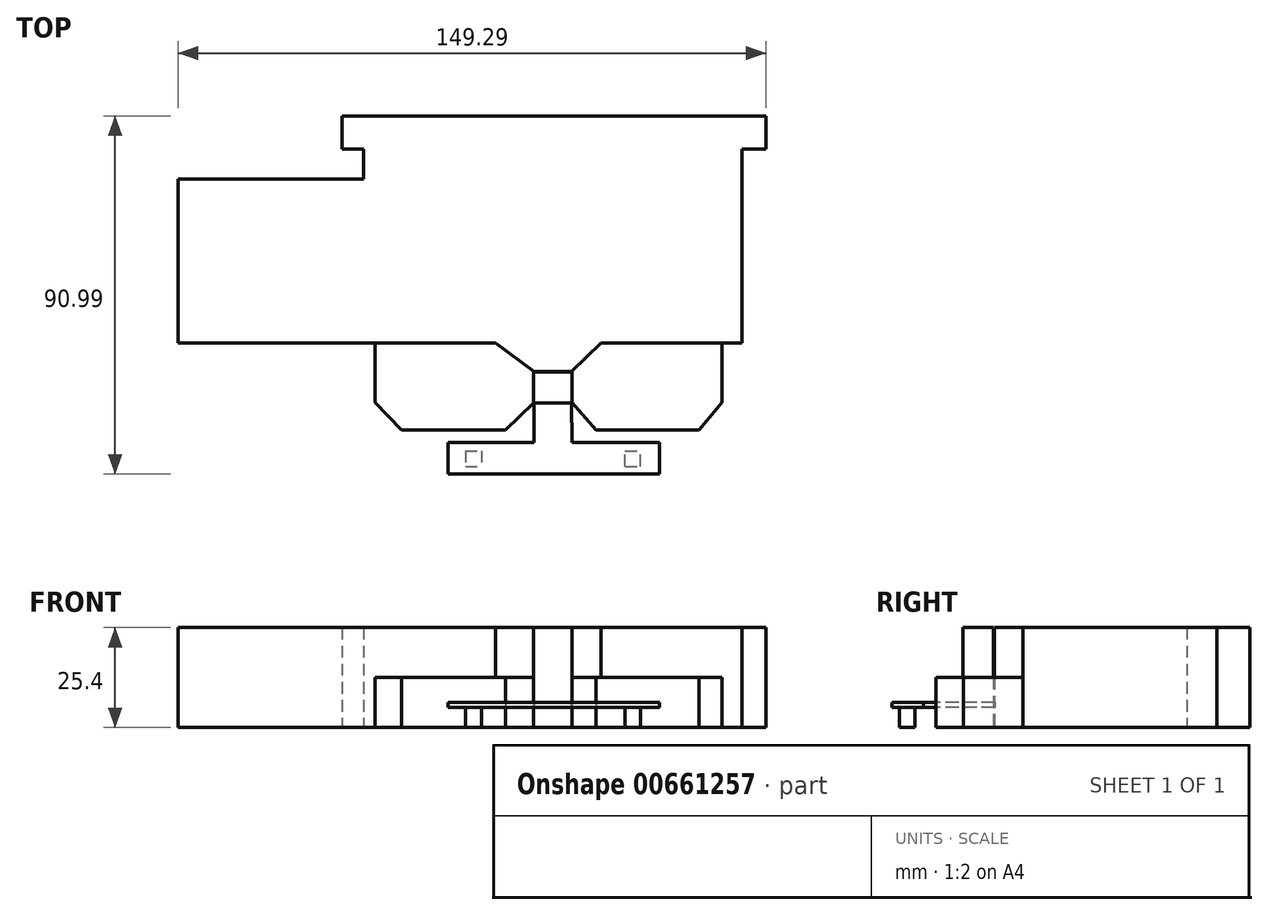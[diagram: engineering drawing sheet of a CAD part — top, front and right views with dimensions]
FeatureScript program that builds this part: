
annotation { "Feature Type Name" : "Feature", "Feature Type Description" : "" }
export const myFeature = defineFeature(function(context is Context, id is Id, definition is map)
    precondition{}
    {
        {
            var Q0;
            Q0=qCreatedBy(makeId("Top.planeOp"),FACE);
            var sketch = newSketch(context, id + "F0", { "sketchPlane" : qUnion([Q0])});
            skLineSegment(sketch, "E0.bottom", {"start": v(-72.94, 27.77) * mm, "end": v(70.25, 27.77) * mm});
            skLineSegment(sketch, "E0.top", {"start": v(-72.94, -13.88) * mm, "end": v(70.25, -13.88) * mm});
            skLineSegment(sketch, "E0.left", {"start": v(-72.94, 27.77) * mm, "end": v(-72.94, -13.88) * mm});
            skLineSegment(sketch, "E0.right", {"start": v(70.25, 27.77) * mm, "end": v(70.25, -13.88) * mm});
            skLineSegment(sketch, "E1", {"start": v(-25.82, 27.77) * mm, "end": v(-25.82, 35.39) * mm});
            skLineSegment(sketch, "E2", {"start": v(-25.82, 35.39) * mm, "end": v(-31.29, 35.39) * mm});
            skLineSegment(sketch, "E3", {"start": v(-31.29, 35.39) * mm, "end": v(-31.29, 43.84) * mm});
            skLineSegment(sketch, "E4", {"start": v(-31.29, 43.84) * mm, "end": v(76.35, 43.84) * mm});
            skLineSegment(sketch, "E5", {"start": v(76.35, 43.84) * mm, "end": v(76.35, 35.39) * mm});
            skLineSegment(sketch, "E6", {"start": v(76.35, 35.39) * mm, "end": v(70.25, 35.39) * mm});
            skLineSegment(sketch, "E7", {"start": v(70.25, 35.39) * mm, "end": v(70.25, 27.77) * mm});
            skLineSegment(sketch, "E8", {"start": v(10.44, -13.88) * mm, "end": v(17.43, -21.12) * mm});
            skLineSegment(sketch, "E9", {"start": v(17.43, -21.12) * mm, "end": v(27.03, -21.12) * mm});
            skLineSegment(sketch, "E10", {"start": v(27.03, -21.12) * mm, "end": v(33.14, -13.88) * mm});
            skLineSegment(sketch, "E11", {"start": v(33.14, -13.88) * mm, "end": v(70.25, -13.88) * mm});
            skLineSegment(sketch, "E12", {"start": v(27.03, -21.12) * mm, "end": v(27.03, -28.97) * mm});
            skLineSegment(sketch, "E13", {"start": v(27.03, -28.97) * mm, "end": v(33.14, -35.96) * mm});
            skLineSegment(sketch, "E14", {"start": v(33.14, -35.96) * mm, "end": v(59.33, -35.96) * mm});
            skLineSegment(sketch, "E15", {"start": v(59.33, -35.96) * mm, "end": v(65.23, -28.97) * mm});
            skLineSegment(sketch, "E16", {"start": v(65.23, -28.97) * mm, "end": v(65.23, -13.88) * mm});
            skLineSegment(sketch, "E17", {"start": v(17.43, -21.12) * mm, "end": v(17.43, -28.97) * mm});
            skLineSegment(sketch, "E18", {"start": v(17.43, -28.97) * mm, "end": v(10.2, -35.96) * mm});
            skLineSegment(sketch, "E19", {"start": v(10.2, -35.96) * mm, "end": v(-16.18, -35.96) * mm});
            skPoint(sketch, "E19.endSnap0", {"position": v(46.24, -35.96) * mm});
            skLineSegment(sketch, "E20", {"start": v(-16.18, -35.96) * mm, "end": v(-22.92, -28.97) * mm});
            skLineSegment(sketch, "E21", {"start": v(-22.92, -28.97) * mm, "end": v(-22.92, -13.88) * mm});
            skSolve(sketch);
        }
        {
            var Q0;
            Q0 = qSketchRegion(id + "F0", true);
            extrude(context, id + "F1", {"entities" : qUnion([Q0]), "depth" : 12.7 * mm, "offsetDistance" : 25.4 * mm});
        }
        {
            var Q0;
            Q0=makeQuery(id+"F1.opExtrude","CAP_FACE",FACE,{"disambiguationData":[OSD([sQuery(id+"F0.wireOp",EDGE,"E0.bottom"),sQuery(id+"F0.wireOp",EDGE,"E0.top"),sQuery(id+"F0.wireOp",EDGE,"E0.left"),sQuery(id+"F0.wireOp",EDGE,"E0.right"),sQuery(id+"F0.wireOp",EDGE,"E1"),sQuery(id+"F0.wireOp",EDGE,"E2"),sQuery(id+"F0.wireOp",EDGE,"E3"),sQuery(id+"F0.wireOp",EDGE,"E4"),sQuery(id+"F0.wireOp",EDGE,"E5"),sQuery(id+"F0.wireOp",EDGE,"E6"),sQuery(id+"F0.wireOp",EDGE,"E7"),sQuery(id+"F0.wireOp",EDGE,"E9"),sQuery(id+"F0.wireOp",EDGE,"E11"),sQuery(id+"F0.wireOp",EDGE,"E12"),sQuery(id+"F0.wireOp",EDGE,"E13"),sQuery(id+"F0.wireOp",EDGE,"E14"),sQuery(id+"F0.wireOp",EDGE,"E15"),sQuery(id+"F0.wireOp",EDGE,"E16"),sQuery(id+"F0.wireOp",EDGE,"E17"),sQuery(id+"F0.wireOp",EDGE,"E18"),sQuery(id+"F0.wireOp",EDGE,"E19"),sQuery(id+"F0.wireOp",EDGE,"E20"),sQuery(id+"F0.wireOp",EDGE,"E21")])],"isStart":false});
            var sketch = newSketch(context, id + "F2", { "sketchPlane" : qUnion([Q0])});
            skLineSegment(sketch, "E22", {"start": v(-22.92, -13.88) * mm, "end": v(7.63, -13.88) * mm});
            skLineSegment(sketch, "E23", {"start": v(7.63, -13.88) * mm, "end": v(17.43, -21.12) * mm});
            skLineSegment(sketch, "E24", {"start": v(17.43, -21.12) * mm, "end": v(27.03, -21.12) * mm});
            skLineSegment(sketch, "E25", {"start": v(27.03, -21.12) * mm, "end": v(34.42, -13.88) * mm});
            skLineSegment(sketch, "E26", {"start": v(34.42, -13.88) * mm, "end": v(65.23, -13.88) * mm});
            skLineSegment(sketch, "E27", {"start": v(65.23, -13.88) * mm, "end": v(70.25, -13.88) * mm});
            skLineSegment(sketch, "E28", {"start": v(70.25, -13.88) * mm, "end": v(70.25, 35.39) * mm});
            skLineSegment(sketch, "E29", {"start": v(70.25, 35.39) * mm, "end": v(76.35, 35.39) * mm});
            skLineSegment(sketch, "E30", {"start": v(76.35, 35.39) * mm, "end": v(76.35, 43.84) * mm});
            skLineSegment(sketch, "E31", {"start": v(76.35, 43.84) * mm, "end": v(-31.29, 43.84) * mm});
            skLineSegment(sketch, "E32", {"start": v(-31.29, 43.84) * mm, "end": v(-31.29, 35.39) * mm});
            skLineSegment(sketch, "E33", {"start": v(-31.29, 35.39) * mm, "end": v(-25.82, 35.39) * mm});
            skLineSegment(sketch, "E34", {"start": v(-25.82, 35.39) * mm, "end": v(-25.82, 27.77) * mm});
            skLineSegment(sketch, "E35", {"start": v(-25.82, 27.77) * mm, "end": v(-72.94, 27.77) * mm});
            skLineSegment(sketch, "E36", {"start": v(-72.94, 27.77) * mm, "end": v(-72.94, -13.88) * mm});
            skLineSegment(sketch, "E37", {"start": v(-72.94, -13.88) * mm, "end": v(-22.92, -13.88) * mm});
            skSolve(sketch);
        }
        {
            var Q0;
            Q0=makeQuery(id+"F2.imprint","IMPRINT",FACE,{"disambiguationData":[TD([[makeQuery(id+"F2.imprint","IMPRINT",EDGE,{"derivedFrom":sQuery(id+"F2.wireOp",EDGE,"E22")}),1.0]])]});
            extrude(context, id + "F3", {"entities" : qUnion([Q0]), "operationType" : NewBodyOperationType.ADD, "depth" : 12.7 * mm, "offsetDistance" : 25.4 * mm});
        }
        {
            var Q0;
            Q0=qCreatedBy(makeId("Top.planeOp"),FACE);
            var sketch = newSketch(context, id + "F4", { "sketchPlane" : qUnion([Q0])});
            skLineSegment(sketch, "E38.bottom", {"start": v(0, -41.26) * mm, "end": v(4.11, -41.26) * mm});
            skLineSegment(sketch, "E38.top", {"start": v(0, -45.19) * mm, "end": v(4.11, -45.19) * mm});
            skLineSegment(sketch, "E38.left", {"start": v(0, -41.26) * mm, "end": v(0, -45.19) * mm});
            skLineSegment(sketch, "E38.right", {"start": v(4.11, -41.26) * mm, "end": v(4.11, -45.19) * mm});
            skLineSegment(sketch, "E39.bottom", {"start": v(40.57, -45.19) * mm, "end": v(44.5, -45.19) * mm});
            skLineSegment(sketch, "E39.top", {"start": v(40.57, -41.26) * mm, "end": v(44.5, -41.26) * mm});
            skLineSegment(sketch, "E39.left", {"start": v(40.57, -45.19) * mm, "end": v(40.57, -41.26) * mm});
            skLineSegment(sketch, "E39.right", {"start": v(44.5, -45.19) * mm, "end": v(44.5, -41.26) * mm});
            skSolve(sketch);
        }
        {
            var Q0;
            Q0 = qSketchRegion(id + "F4", true);
            extrude(context, id + "F5", {"entities" : qUnion([Q0]), "depth" : 5.08 * mm, "offsetDistance" : 25.4 * mm});
        }
        {
            var Q0;
            Q0=makeQuery(id+"F5.opExtrude","CAP_FACE",FACE,{"disambiguationData":[OSD([sQuery(id+"F4.wireOp",EDGE,"E38.bottom"),sQuery(id+"F4.wireOp",EDGE,"E38.top"),sQuery(id+"F4.wireOp",EDGE,"E38.left"),sQuery(id+"F4.wireOp",EDGE,"E38.right")])],"isStart":false});
            var sketch = newSketch(context, id + "F6", { "sketchPlane" : qUnion([Q0])});
            skLineSegment(sketch, "E40", {"start": v(17.43, -20.96) * mm, "end": v(17.43, -37.33) * mm});
            skLineSegment(sketch, "E41", {"start": v(17.43, -37.33) * mm, "end": v(17.43, -39.08) * mm});
            skLineSegment(sketch, "E42", {"start": v(17.43, -39.08) * mm, "end": v(-4.4, -39.08) * mm});
            skLineSegment(sketch, "E43", {"start": v(-4.4, -39.08) * mm, "end": v(-4.4, -47.15) * mm});
            skLineSegment(sketch, "E44", {"start": v(-4.4, -47.15) * mm, "end": v(49.3, -47.15) * mm});
            skLineSegment(sketch, "E45", {"start": v(49.3, -47.15) * mm, "end": v(49.3, -39.08) * mm});
            skLineSegment(sketch, "E46", {"start": v(49.3, -39.08) * mm, "end": v(27.04, -39.08) * mm});
            skLineSegment(sketch, "E47", {"start": v(26.82, -21.4) * mm, "end": v(27.04, -39.08) * mm});
            skLineSegment(sketch, "E48", {"start": v(26.82, -21.4) * mm, "end": v(17.43, -20.96) * mm});
            skSolve(sketch);
        }
        {
            var Q0;
            Q0 = qSketchRegion(id + "F6", true);
            extrude(context, id + "F7", {"entities" : qUnion([Q0]), "depth" : 1.27 * mm, "offsetDistance" : 25.4 * mm});
        }
        {
            var Q0;
            Q0=qCreatedBy(makeId("Top.planeOp"),FACE);
            var sketch = newSketch(context, id + "F8", { "sketchPlane" : qUnion([Q0])});
            skLineSegment(sketch, "E49.bottom", {"start": v(17.33, -21.27) * mm, "end": v(27.06, -21.27) * mm});
            skLineSegment(sketch, "E49.top", {"start": v(17.33, -29.1) * mm, "end": v(27.06, -29.1) * mm});
            skLineSegment(sketch, "E49.left", {"start": v(17.33, -21.27) * mm, "end": v(17.33, -29.1) * mm});
            skLineSegment(sketch, "E49.right", {"start": v(27.06, -21.27) * mm, "end": v(27.06, -29.1) * mm});
            skSolve(sketch);
        }
        {
            var Q0;
            Q0=makeQuery(id+"F8.imprint","IMPRINT",FACE,{"disambiguationData":[TD([[makeQuery(id+"F8.imprint","IMPRINT",EDGE,{"derivedFrom":sQuery(id+"F8.wireOp",EDGE,"E49.bottom")}),-1.0]])]});
            extrude(context, id + "F9", {"entities" : qUnion([Q0]), "depth" : 25.4 * mm, "offsetDistance" : 25.4 * mm});
        }
    });
